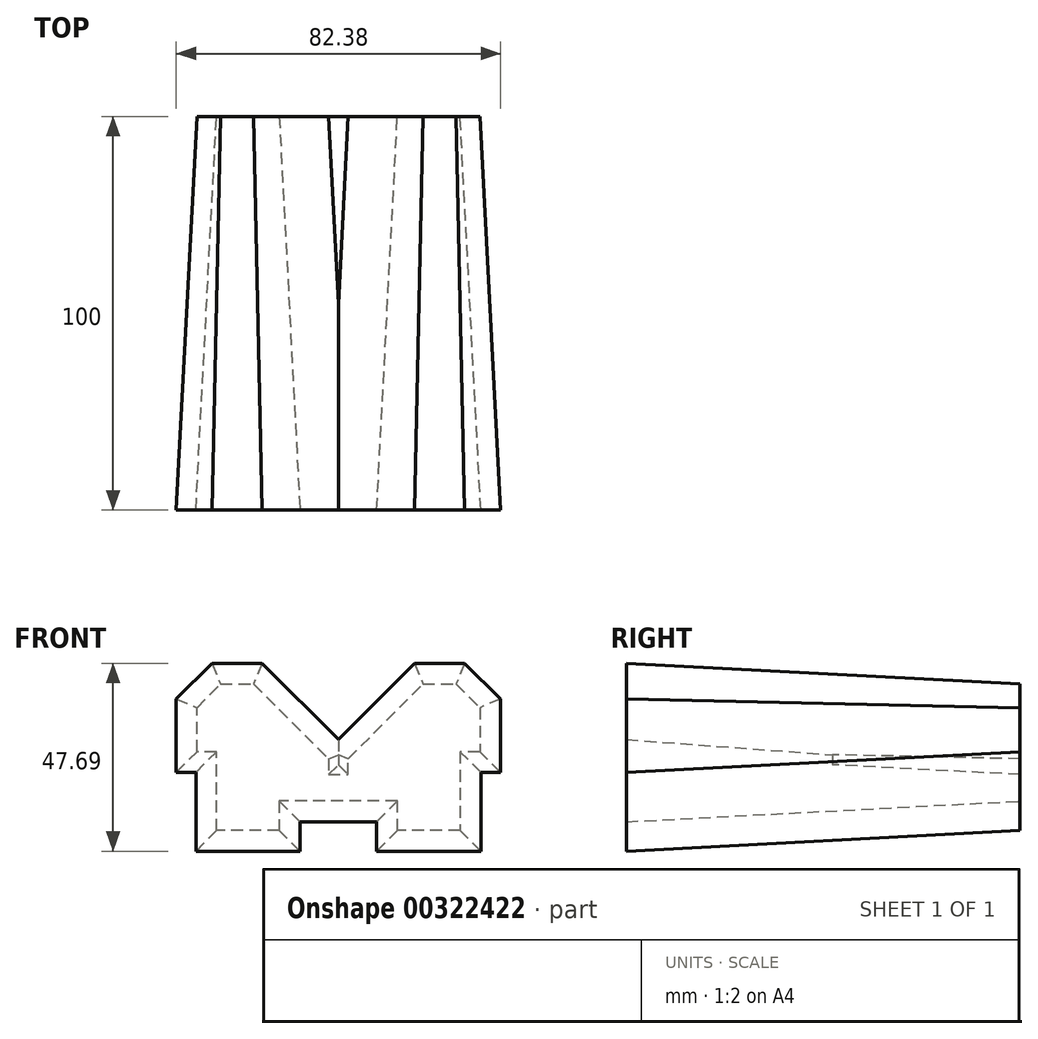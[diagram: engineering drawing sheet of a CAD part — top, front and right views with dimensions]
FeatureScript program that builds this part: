
annotation { "Feature Type Name" : "Feature", "Feature Type Description" : "" }
export const myFeature = defineFeature(function(context is Context, id is Id, definition is map)
    precondition{}
    {
        {
            var Q0;
            Q0=qCreatedBy(makeId("Front.planeOp"),FACE);
            var sketch = newSketch(context, id + "F0", { "sketchPlane" : qUnion([Q0])});
            skLineSegment(sketch, "E0", {"start": v(0, -8.5) * mm, "end": v(-15, -8.5) * mm});
            skLineSegment(sketch, "E1", {"start": v(-15, -8.5) * mm, "end": v(-15, -15.97) * mm});
            skLineSegment(sketch, "E2", {"start": v(-15, -15.97) * mm, "end": v(-30.95, -15.97) * mm});
            skLineSegment(sketch, "E3", {"start": v(-30.95, -15.97) * mm, "end": v(-30.95, 4.03) * mm});
            skLineSegment(sketch, "E4", {"start": v(-30.95, 4.03) * mm, "end": v(-35.95, 4.03) * mm});
            skLineSegment(sketch, "E5", {"start": v(-35.95, 4.03) * mm, "end": v(-35.95, 15.24) * mm});
            skLineSegment(sketch, "E6", {"start": v(-35.95, 15.24) * mm, "end": v(-29.95, 21.24) * mm});
            skLineSegment(sketch, "E7", {"start": v(-29.95, 21.24) * mm, "end": v(-21.5, 21.24) * mm});
            skPoint(sketch, "E8.end.orphan", {"position": v(15, -8.5) * mm});
            skPoint(sketch, "E9.start.orphan", {"position": v(0, 0) * mm});
            skLineSegment(sketch, "E10.MirrorCS", {"start": v(0, -8.5) * mm, "end": v(15, -8.5) * mm});
            skLineSegment(sketch, "E11.MirrorCS", {"start": v(15, -15.97) * mm, "end": v(30.95, -15.97) * mm});
            skLineSegment(sketch, "E12.MirrorCS", {"start": v(30.95, 4.03) * mm, "end": v(35.95, 4.03) * mm});
            skLineSegment(sketch, "E13.MirrorCS", {"start": v(35.95, 4.03) * mm, "end": v(35.95, 15.24) * mm});
            skLineSegment(sketch, "E14.MirrorCS", {"start": v(35.95, 15.24) * mm, "end": v(29.95, 21.24) * mm});
            skLineSegment(sketch, "E15.MirrorCS", {"start": v(29.95, 21.24) * mm, "end": v(21.5, 21.24) * mm});
            skLineSegment(sketch, "E16.MirrorCS", {"start": v(30.95, -15.97) * mm, "end": v(30.95, 4.03) * mm});
            skLineSegment(sketch, "E17.MirrorCS", {"start": v(15, -8.5) * mm, "end": v(15, -15.97) * mm});
            skPoint(sketch, "E18.start.orphan", {"position": v(-2.5, 0) * mm});
            skPoint(sketch, "E19.end.orphan", {"position": v(0, -2.69) * mm});
            skPoint(sketch, "E19.start.orphan", {"position": v(-2.5, -2.69) * mm});
            skPoint(sketch, "E20.MirrorCS.end.orphan", {"position": v(2.5, 0) * mm});
            skPoint(sketch, "E20.MirrorCS.start.orphan", {"position": v(21.5, 21.24) * mm});
            skPoint(sketch, "E21.end.orphan", {"position": v(2.08, 2.94) * mm});
            skPoint(sketch, "E21.start.orphan", {"position": v(7.08, 2.94) * mm});
            skPoint(sketch, "E22.end.orphan", {"position": v(0, 8.99) * mm});
            skLineSegment(sketch, "E23", {"start": v(-21.5, 21.24) * mm, "end": v(-2.5, 2.24) * mm});
            skLineSegment(sketch, "E24", {"start": v(-2.5, -1.76) * mm, "end": v(-2.5, 2.24) * mm});
            skPoint(sketch, "E25.start.orphan", {"position": v(2.5, 8.99) * mm});
            skLineSegment(sketch, "E26.MirrorCS", {"start": v(21.5, 21.24) * mm, "end": v(2.5, 2.24) * mm});
            skLineSegment(sketch, "E27", {"start": v(-2.5, -1.76) * mm, "end": v(2.5, -1.76) * mm});
            skLineSegment(sketch, "E28", {"start": v(2.5, -1.76) * mm, "end": v(2.5, 2.24) * mm});
            skSolve(sketch);
        }
        {
            var Q0;
            Q0=makeQuery(id+"F0.imprint","IMPRINT",FACE,{"disambiguationData":[TD([[makeQuery(id+"F0.imprint","IMPRINT",EDGE,{"derivedFrom":sQuery(id+"F0.wireOp",EDGE,"E0")}),-1.0]])]});
            extrude(context, id + "F1", {"entities" : qUnion([Q0]), "depth" : 100 * mm, "hasDraft" : true, "draftAngle" : 3 * degree});
        }
    });
